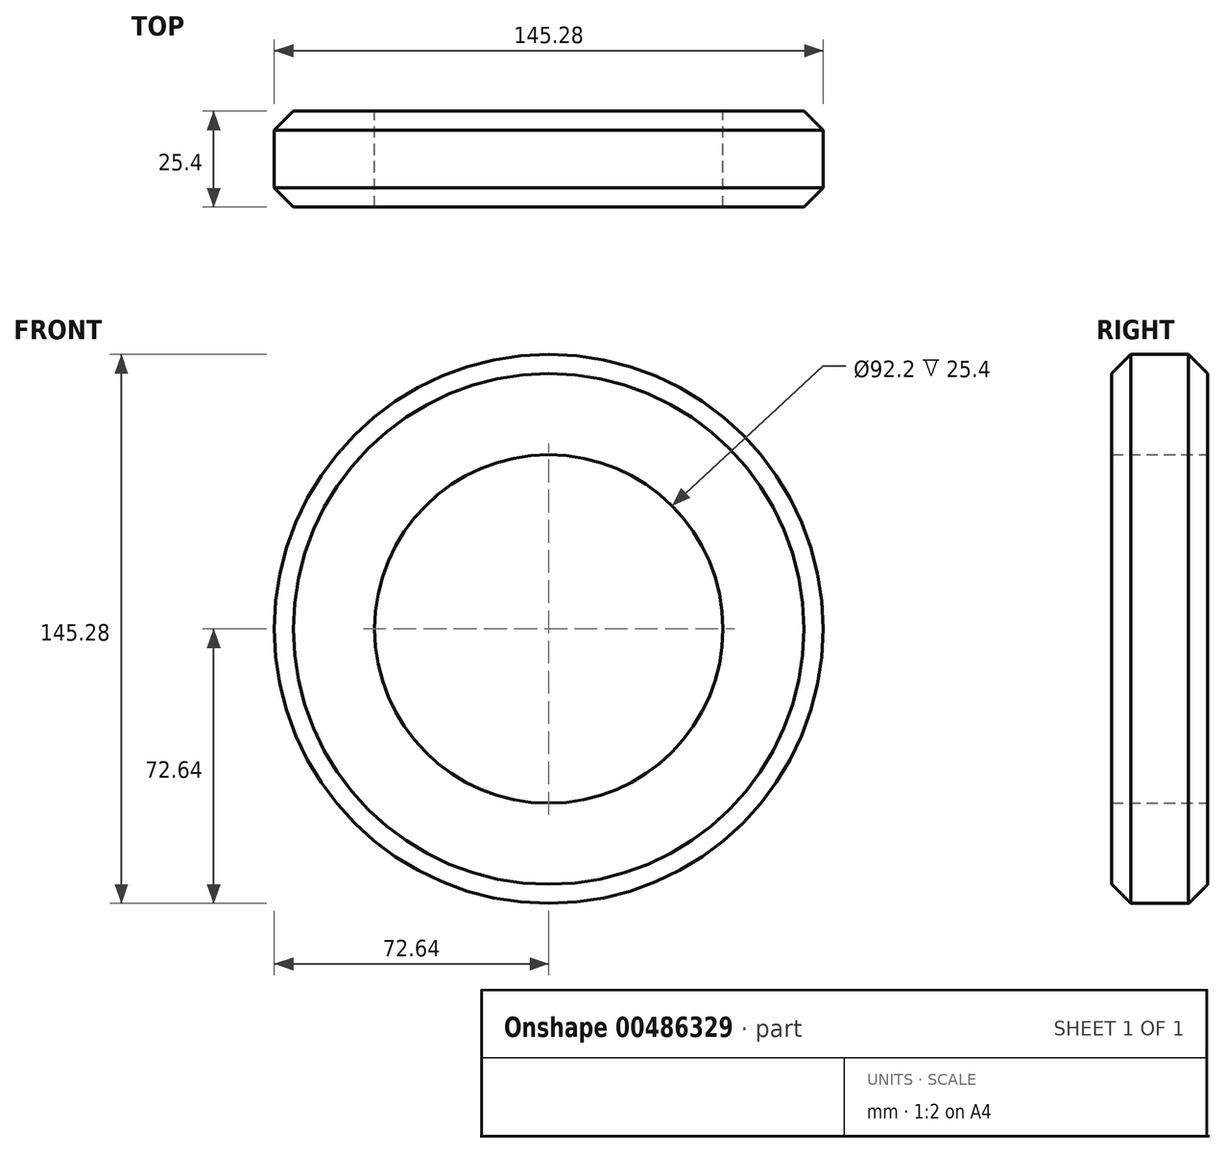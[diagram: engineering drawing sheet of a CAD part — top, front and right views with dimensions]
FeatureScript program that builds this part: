
annotation { "Feature Type Name" : "Feature", "Feature Type Description" : "" }
export const myFeature = defineFeature(function(context is Context, id is Id, definition is map)
    precondition{}
    {
        {
            var Q0;
            Q0=qCreatedBy(makeId("Front.planeOp"),FACE);
            var sketch = newSketch(context, id + "F0", { "sketchPlane" : qUnion([Q0])});
            skCircle(sketch, "E0", {"center": v(0, 0) * mm, "radius": 72.64 * mm});
            skSolve(sketch);
        }
        {
            var Q0;
            Q0=makeQuery(id+"F0.imprint","IMPRINT",FACE,{"disambiguationData":[TD([[makeQuery(id+"F0.imprint","IMPRINT",EDGE,{"derivedFrom":sQuery(id+"F0.wireOp",EDGE,"E0")}),1.0]])]});
            var sketch = newSketch(context, id + "F1", { "sketchPlane" : qUnion([Q0])});
            skCircle(sketch, "E1", {"center": v(0, 0) * mm, "radius": 46.1 * mm});
            skSolve(sketch);
        }
        {
            var Q0;
            Q0=makeQuery(id+"F1.imprint","IMPRINT",FACE,{"disambiguationData":[TD([[makeQuery(id+"F1.imprint","IMPRINT",EDGE,{"derivedFrom":sQuery(id+"F1.wireOp",EDGE,"E1")}),-1.0]])]});
            extrude(context, id + "F2", {"entities" : qUnion([Q0]), "depth" : 25.4 * mm});
        }
        {
            var Q0;
            Q0=makeQuery(id+"F2.opExtrude","SWEPT_FACE",FACE,{"disambiguationData":[OSD([sQuery(id+"F0.wireOp",EDGE,"E0")])]});
            chamfer(context, id + "F3", {"entities" : qUnion([Q0]), "width" : 5.08 * mm, "tangentPropagation" : true});
        }
    });
